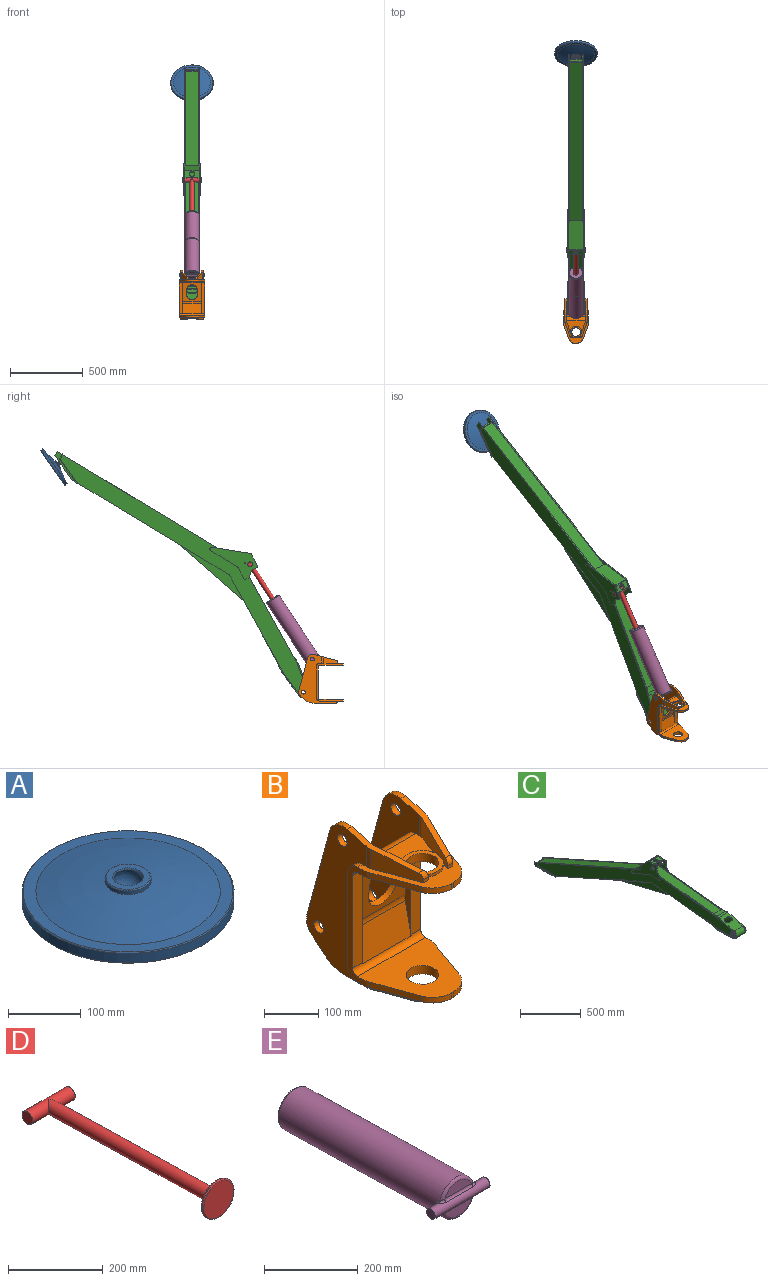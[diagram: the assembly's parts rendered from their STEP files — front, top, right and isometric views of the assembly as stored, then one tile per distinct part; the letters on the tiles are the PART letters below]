
ASSEMBLY  parts=5 mates=5
PART A: 11 faces, bbox 292.1x292.1x54.5 mm
  f0: plane 289.15x289.15mm, normal (0,0,-1), area 65666.8mm2, adj f7
  f1: cylinder r=146.05mm len=292.1mm, axis (0,0,1), area 14777.2mm2, adj f7,f8
  f2: plane 289.15x289.15mm, normal (0,0,1), area 14996mm2, adj f3,f8
  f3: revolved ~254x254mm, area 48420.7mm2, adj f2,f4
  f4: cylinder r=31.75mm len=63.5mm, axis (0,0,1), area 1255.8mm2, adj f3,f9
  f5: plane 60.55x60.55mm, normal (0,0,1), area 1477.2mm2, adj f9,f10
  f6: sphere r=21.59mm, area 4102.8mm2, adj f10
  f7: cone r=146.05mm half-angle=45deg, axis (0,0,1), area 1902.5mm2, adj f0,f1
  f8: cone r=144.58mm half-angle=45deg, axis (0,0,-1), area 1902.5mm2, adj f1,f2
  f9: cone r=30.28mm half-angle=45deg, axis (0,0,-1), area 406mm2, adj f4,f5
  f10: cone r=19.78mm half-angle=33.2deg, axis (0,0,1), area 317mm2, adj f5,f6
PART B: 98 faces, bbox 177.8x305.8x334 mm
  f0: plane 213.74x16.26mm, normal (1,0,0), area 1741.2mm2, adj f36,f38,f39,f87,f88,f89
  f1: plane 334.04x155.74mm, normal (1,0,0), area 29123.4mm2, adj f6,f7,f8,f10,f11,f12,f13,f14
  f2: plane 334.04x155.74mm, normal (-1,0,0), area 29123.4mm2, adj f40,f42,f67,f68,f72,f73,f74,f75
  f3: plane 213.74x16.26mm, normal (-1,0,0), area 1741.2mm2, adj f4,f38,f39,f87,f88,f89
  f4: plane 209.55x25.4mm, normal (0,-1,0), area 5322.6mm2, adj f3,f32,f38,f39
  f5: plane 103.39x44.26mm, normal (0.94,0.34,0), area 3175.5mm2, adj f8,f9,f22,f24,f25,f40,f47,f48
  f6: cylinder r=12.7mm len=25.4mm, axis (-1,0,0), area 1013.4mm2, adj f1,f16
  f7: cylinder r=12.7mm len=25.4mm, axis (-1,0,0), area 1013.4mm2, adj f1,f16
  f8: plane 151.55x48mm, normal (0,-0.26,0.97), area 2071.1mm2, adj f1,f5,f10,f16,f18,f19,f22,f94
  f9: plane 13.5x6.81mm, normal (0,-1,0), area 92mm2, adj f5,f19,f24,f94
  f10: cylinder r=38.1mm len=46.66mm, axis (-1,0,0), area 760.1mm2, adj f1,f8,f11,f16
  f11: plane 219.46x58.81mm, normal (0,0.97,0.26), area 2885.5mm2, adj f1,f10,f12,f16
  f12: cylinder r=38.1mm len=39.05mm, axis (-1,0,0), area 548.9mm2, adj f1,f11,f13,f16
  f13: plane 35.11x29.46mm, normal (0,0.64,-0.77), area 582.1mm2, adj f1,f12,f14,f16
  f14: cylinder r=76.2mm len=48.98mm, axis (-1,0,0), area 675.6mm2, adj f1,f13,f15,f16
  f15: plane 157.33x46.82mm, normal (0,0,-1), area 2071.4mm2, adj f1,f14,f16,f17,f20,f21,f23,f95
  f16: plane 334.04x155.74mm, normal (-1,0,0), area 30898mm2, adj f6,f7,f8,f10,f11,f12,f13,f14
  f17: cylinder r=38.1mm len=12.9mm, axis (0,0,-1), area 167.1mm2, adj f15,f16,f20,f26
  f18: cylinder r=38.1mm len=46.56mm, axis (0,0,-1), area 589.6mm2, adj f8,f16,f19,f24
  f19: plane 99.09x43.11mm, normal (-0.94,-0.34,0), area 3122.2mm2, adj f8,f9,f18,f24,f94
  f20: plane 99.09x35.64mm, normal (-0.94,-0.34,0), area 1300.6mm2, adj f15,f17,f26,f95
  f21: cylinder r=25.4mm len=12.7mm, axis (0,0,-1), area 111.4mm2, adj f1,f15,f23,f42
  f22: cylinder r=25.4mm len=46.56mm, axis (0,0,-1), area 398.2mm2, adj f1,f5,f8,f40
  f23: plane 103.39x37.19mm, normal (0.94,0.34,0), area 1212.3mm2, adj f15,f21,f26,f27,f42,f49,f50,f95
  f24: plane 177.8x159.66mm, normal (0,0,1), area 6507mm2, adj f5,f9,f16,f18,f19,f25,f29,f32
  f25: cylinder r=38.89mm len=62.11mm, axis (0,0,-1), area 456.7mm2, adj f5,f24,f48,f63
  f26: plane 177.8x159.66mm, normal (0,0,-1), area 6507mm2, adj f16,f17,f20,f23,f30,f31,f32,f34
  f27: cylinder r=38.89mm len=77.78mm, axis (0,0,1), area 797.8mm2, adj f23,f42,f50,f69
  f28: plane 209.55x12.7mm, normal (0,1,0), area 2661.3mm2, adj f29,f30,f32,f80
  f29: cylinder r=25.4mm len=25.4mm, axis (-1,0,0), area 506.7mm2, adj f24,f28,f32,f80
  f30: cylinder r=25.4mm len=25.4mm, axis (-1,0,0), area 506.7mm2, adj f26,f28,f32,f80
  f31: plane 12.7x4.77mm, normal (0,-1,0), area 60.6mm2, adj f26,f37,f59,f60
  f32: plane 260.35x34.98mm, normal (1,0,0), area 3664.7mm2, adj f4,f24,f26,f28,f29,f30,f35,f37
  f33: plane 12.7x4.77mm, normal (0,-1,0), area 60.6mm2, adj f24,f35,f55,f56
  f34: plane 260.35x34.98mm, normal (-1,0,0), area 3664.7mm2, adj f24,f26,f35,f36,f37,f38,f39,f41
  f35: plane 177.8x159.66mm, normal (0,0,-1), area 17911.7mm2, adj f32,f33,f34,f38,f46,f53,f54,f55
  f36: plane 209.55x25.4mm, normal (0,-1,0), area 5322.6mm2, adj f0,f34,f38,f39
  f37: plane 177.8x159.66mm, normal (0,0,1), area 17911.7mm2, adj f31,f32,f34,f39,f45,f51,f52,f57
  f38: cylinder r=12.7mm len=177.8mm, axis (-1,0,0), area 3349.9mm2, adj f0,f3,f4,f32,f34,f35,f36,f89
  f39: cylinder r=12.7mm len=177.8mm, axis (-1,0,0), area 3209.1mm2, adj f0,f3,f4,f32,f34,f36,f37,f87
  f40: plane 127x82.53mm, normal (0,0,1), area 6280mm2, adj f1,f2,f5,f22,f47,f63,f67,f85
  f41: plane 209.55x12.7mm, normal (0,1,0), area 2661.3mm2, adj f16,f34,f43,f44
  f42: plane 127x82.53mm, normal (0,0,-1), area 6280mm2, adj f1,f2,f21,f23,f27,f68,f69,f86
  f43: cylinder r=25.4mm len=25.4mm, axis (-1,0,0), area 506.7mm2, adj f16,f24,f34,f41
  f44: cylinder r=25.4mm len=25.4mm, axis (-1,0,0), area 506.7mm2, adj f16,f26,f34,f41
  f45: cylinder r=30mm len=60mm, axis (0,0,1), area 3590.8mm2, adj f37,f50
  f46: cylinder r=30mm len=60mm, axis (0,0,1), area 3590.8mm2, adj f35,f48
  f47: cylinder r=38.89mm len=77.78mm, axis (0,0,-1), area 797.8mm2, adj f5,f40,f48,f63
  f48: plane 77.78x77.78mm, normal (0,0,1), area 1870.2mm2, adj f5,f25,f46,f47,f63
  f49: cylinder r=38.89mm len=62.11mm, axis (0,0,1), area 456.7mm2, adj f23,f26,f50,f69
  f50: plane 77.78x77.78mm, normal (0,0,-1), area 1870.2mm2, adj f23,f27,f45,f49,f69
  f51: plane 99.28x35.71mm, normal (-0.94,-0.34,0), area 1340mm2, adj f26,f37,f59,f61
  f52: plane 99.28x35.71mm, normal (0.94,-0.34,0), area 1340mm2, adj f26,f37,f57,f60
  f53: plane 99.28x35.71mm, normal (-0.94,-0.34,0), area 1340mm2, adj f24,f35,f55,f62
  f54: plane 99.28x35.71mm, normal (0.94,-0.34,0), area 1340mm2, adj f24,f35,f56,f58
  f55: cylinder r=50.8mm len=47.8mm, axis (0,0,1), area 790.6mm2, adj f24,f33,f35,f53
  f56: cylinder r=50.8mm len=47.8mm, axis (0,0,1), area 790.6mm2, adj f24,f33,f35,f54
  f57: cylinder r=50.8mm len=17.19mm, axis (0,0,1), area 222.8mm2, adj f26,f32,f37,f52
  f58: cylinder r=50.8mm len=17.19mm, axis (0,0,-1), area 222.8mm2, adj f24,f32,f35,f54
  f59: cylinder r=50.8mm len=47.8mm, axis (0,0,1), area 790.6mm2, adj f26,f31,f37,f51
  f60: cylinder r=50.8mm len=47.8mm, axis (0,0,1), area 790.6mm2, adj f26,f31,f37,f52
  f61: cylinder r=50.8mm len=17.19mm, axis (0,0,-1), area 222.8mm2, adj f26,f34,f37,f51
  f62: cylinder r=50.8mm len=17.19mm, axis (0,0,1), area 222.8mm2, adj f24,f34,f35,f53
  f63: plane 103.39x44.26mm, normal (-0.94,0.34,0), area 3175.5mm2, adj f24,f25,f40,f47,f48,f66,f67,f77
  f64: cylinder r=38.1mm len=46.56mm, axis (0,0,-1), area 589.6mm2, adj f24,f65,f77,f80
  f65: plane 99.09x43.11mm, normal (0.94,-0.34,0), area 3122.2mm2, adj f24,f64,f66,f77,f96
  f66: plane 13.5x6.81mm, normal (0,-1,0), area 92mm2, adj f24,f63,f65,f96
  f67: cylinder r=25.4mm len=46.56mm, axis (0,0,-1), area 398.2mm2, adj f2,f40,f63,f77
  f68: cylinder r=25.4mm len=12.7mm, axis (0,0,-1), area 111.4mm2, adj f2,f42,f69,f78
  f69: plane 103.39x37.19mm, normal (-0.94,0.34,0), area 1212.3mm2, adj f26,f27,f42,f49,f50,f68,f78,f97
  f70: plane 99.09x35.64mm, normal (0.94,-0.34,0), area 1300.6mm2, adj f26,f71,f78,f97
  f71: cylinder r=38.1mm len=12.9mm, axis (0,0,-1), area 167.1mm2, adj f26,f70,f78,f80
  f72: cylinder r=76.2mm len=48.98mm, axis (-1,0,0), area 675.6mm2, adj f2,f73,f78,f80
  f73: plane 35.11x29.46mm, normal (0,0.64,-0.77), area 582.1mm2, adj f2,f72,f74,f80
  f74: cylinder r=38.1mm len=39.05mm, axis (-1,0,0), area 548.9mm2, adj f2,f73,f75,f80
  f75: plane 219.46x58.81mm, normal (0,0.97,0.26), area 2885.5mm2, adj f2,f74,f76,f80
  f76: cylinder r=38.1mm len=46.66mm, axis (-1,0,0), area 760.1mm2, adj f2,f75,f77,f80
  f77: plane 151.55x48mm, normal (0,-0.26,0.97), area 2071.1mm2, adj f2,f63,f64,f65,f67,f76,f80,f96
  f78: plane 157.33x46.82mm, normal (0,0,-1), area 2071.4mm2, adj f2,f68,f69,f70,f71,f72,f80,f97
  f79: cylinder r=12.7mm len=25.4mm, axis (-1,0,0), area 1013.4mm2, adj f2,f80
  f80: plane 334.04x155.74mm, normal (1,0,0), area 30898mm2, adj f24,f26,f28,f29,f30,f64,f71,f72
  f81: cylinder r=12.7mm len=25.4mm, axis (-1,0,0), area 1013.4mm2, adj f2,f80
  f82: plane 127x72.57mm, normal (0,0.98,-0.21), area 9422.1mm2, adj f1,f2,f83,f86
  f83: cylinder r=50.8mm len=127mm, axis (1,0,0), area 2139.4mm2, adj f1,f2,f82,f84
  f84: plane 128.61x127mm, normal (0,0.99,0.12), area 9763.7mm2, adj f1,f2,f83,f85,f90,f91,f92,f93
  f85: cylinder r=25.4mm len=127mm, axis (1,0,0), area 4673mm2, adj f1,f2,f40,f84
  f86: cylinder r=25.4mm len=127mm, axis (1,0,0), area 4391.5mm2, adj f1,f2,f42,f82
  f87: plane 127x72.57mm, normal (0,-0.98,0.21), area 9422.1mm2, adj f0,f3,f39,f88
  f88: cylinder r=38.1mm len=127mm, axis (1,0,0), area 1604.6mm2, adj f0,f3,f87,f89
  f89: plane 128.61x127mm, normal (0,-0.99,-0.12), area 9763.7mm2, adj f0,f3,f38,f88,f90,f91,f92,f93
  f90: plane 29.31x16.01mm, normal (-1,0,0), area 355.2mm2, adj f84,f89,f91,f93
  f91: cylinder r=38.1mm len=76.2mm, axis (0,0.99,0.12), area 1520.1mm2, adj f84,f89,f90,f92
  f92: plane 29.31x16.01mm, normal (1,0,0), area 355.2mm2, adj f84,f89,f91,f93
  f93: cylinder r=38.1mm len=76.2mm, axis (0,0.99,0.12), area 1520.1mm2, adj f84,f89,f90,f92
  f94: cylinder r=12.7mm len=16.88mm, axis (1,0,0), area 224.4mm2, adj f5,f8,f9,f19
  f95: cylinder r=12.7mm len=18.07mm, axis (1,0,0), area 269.2mm2, adj f15,f20,f23,f26
  f96: cylinder r=12.7mm len=16.88mm, axis (1,0,0), area 224.4mm2, adj f63,f65,f66,f77
  f97: cylinder r=12.7mm len=18.07mm, axis (1,0,0), area 269.2mm2, adj f26,f69,f70,f78
PART C: 172 faces, bbox 127x2358.1x762.4 mm
  f0: cylinder r=9.53mm len=19.05mm, axis (0,0,1), area 271.4mm2, adj f169,f170
  f1: sphere r=12.7mm, area 872.5mm2, adj f170,f171
  f2: plane 2312.35x598.31mm, normal (-1,0,0), area 247360.8mm2, adj f3,f5,f17,f24,f25,f41,f42,f56
  f3: plane 530.06x57.29mm, normal (0,0.11,-0.99), area 3305.6mm2, adj f2,f40,f90,f96,f112
  f4: plane 750.78x331.63mm, normal (0,-0.4,-0.91), area 5211.8mm2, adj f17,f51,f52,f108
  f5: plane 762.53x82.41mm, normal (0,-0.11,0.99), area 4790.4mm2, adj f2,f40,f41,f92,f94,f132
  f6: plane 762.53x82.41mm, normal (0,-0.11,0.99), area 4790.4mm2, adj f51,f52,f53,f93,f95,f131
  f7: plane 25.33x11.19mm, normal (0,-0.4,-0.91), area 175.9mm2, adj f9,f10,f11,f26
  f8: plane 33.6x14.84mm, normal (0,0.4,0.91), area 233.3mm2, adj f9,f10,f12,f28
  f9: plane 238.23x45.76mm, normal (1,0,0), area 3495.7mm2, adj f7,f8,f11,f12,f19,f26,f28
  f10: plane 238.23x45.76mm, normal (-1,0,0), area 3495.7mm2, adj f7,f8,f11,f12,f15,f26,f28
  f11: plane 199.24x6.35mm, normal (0,0,-1), area 1265.2mm2, adj f7,f9,f10,f12
  f12: plane 30.91x13.66mm, normal (0,0.91,-0.4), area 214.6mm2, adj f8,f9,f10,f11
  f13: plane 173.96x88.9mm, normal (0,0,1), area 15464.7mm2, adj f14,f36,f40,f52
  f14: cylinder r=3.17mm len=88.9mm, axis (1,0,0), area 326mm2, adj f13,f16,f40,f52
  f15: cylinder r=9.53mm len=88.9mm, axis (1,0,0), area 977.9mm2, adj f10,f26,f28,f46
  f16: plane 88.9x20.18mm, normal (0,-0.91,0.4), area 1961mm2, adj f14,f30,f40,f52
  f17: plane 200.03x106.68mm, normal (0,0,1), area 1968.3mm2, adj f2,f4,f18,f21,f22,f23,f24,f34
  f18: cylinder r=3.17mm len=2.9mm, axis (1,0,0), area 9.3mm2, adj f17,f23,f25,f51
  f19: cylinder r=9.53mm len=8.71mm, axis (1,0,0), area 27.9mm2, adj f9,f23,f26,f28
  f20: plane 96.52x5.81mm, normal (0,0.4,0.91), area 612.9mm2, adj f25,f28,f166,f167
  f21: plane 220.47x34.81mm, normal (-1,0,0), area 1501.2mm2, adj f17,f22,f24,f25,f26,f27,f28,f167
  f22: plane 106.68x6.35mm, normal (0,-1,0), area 677.4mm2, adj f17,f21,f23,f26
  f23: plane 220.47x34.81mm, normal (1,0,0), area 1501.2mm2, adj f17,f18,f19,f22,f25,f26,f28,f166
  f24: cylinder r=3.17mm len=2.9mm, axis (1,0,0), area 9.3mm2, adj f2,f17,f21,f25
  f25: plane 106.68x31.21mm, normal (0,-0.91,0.4), area 702.6mm2, adj f2,f18,f20,f21,f23,f24,f32,f40
  f26: plane 200.03x106.68mm, normal (0,0,-1), area 18328.7mm2, adj f7,f9,f10,f15,f19,f21,f22,f23
  f27: cylinder r=9.53mm len=8.71mm, axis (1,0,0), area 27.9mm2, adj f21,f26,f28,f45
  f28: plane 106.68x31.21mm, normal (0,0.91,-0.4), area 3228.1mm2, adj f8,f9,f10,f15,f19,f20,f21,f23
  f29: plane 792.4x88.9mm, normal (0,0.11,-0.99), area 70854.5mm2, adj f30,f38,f40,f52
  f30: plane 1309.57x578.45mm, normal (0,-0.4,-0.91), area 127272.8mm2, adj f16,f29,f40,f52
  f31: plane 794.09x88.9mm, normal (0,-0.11,0.99), area 71005.7mm2, adj f32,f38,f40,f52
  f32: plane 1311.13x579.14mm, normal (0,0.4,0.91), area 127424mm2, adj f25,f31,f40,f52
  f33: plane 765.33x88.9mm, normal (0,0.11,-0.99), area 68434.3mm2, adj f34,f37,f40,f52
  f34: plane 1124.23x496.59mm, normal (0,-0.4,-0.91), area 109260.2mm2, adj f17,f33,f40,f52
  f35: plane 767.02x88.9mm, normal (0,-0.11,0.99), area 68585.6mm2, adj f36,f37,f40,f52
  f36: plane 1138.94x503.08mm, normal (0,0.4,0.91), area 110689.5mm2, adj f13,f35,f40,f52
  f37: plane 88.9x6.31mm, normal (0,-0.99,-0.11), area 564.5mm2, adj f33,f35,f40,f52
  f38: plane 88.9x6.31mm, normal (0,-0.99,-0.11), area 564.5mm2, adj f29,f31,f40,f52
  f39: cylinder r=12.7mm len=25.4mm, axis (1,0,0), area 1520.1mm2, adj f40,f57
  f40: plane 2312.35x610.27mm, normal (1,0,0), area 254834.7mm2, adj f3,f5,f13,f14,f16,f17,f25,f29
  f41: plane 1311.91x579.49mm, normal (0,0.4,0.91), area 9107.1mm2, adj f2,f5,f25,f40,f132
  f42: plane 750.78x331.63mm, normal (0,-0.4,-0.91), area 5211.8mm2, adj f2,f17,f40,f112
  f43: plane 25.33x11.19mm, normal (0,-0.4,-0.91), area 175.9mm2, adj f26,f45,f46,f47
  f44: plane 33.6x14.84mm, normal (0,0.4,0.91), area 233.3mm2, adj f28,f45,f46,f48
  f45: plane 238.23x45.76mm, normal (-1,0,0), area 3495.7mm2, adj f26,f27,f28,f43,f44,f47,f48
  f46: plane 238.23x45.76mm, normal (1,0,0), area 3495.7mm2, adj f15,f26,f28,f43,f44,f47,f48
  f47: plane 199.24x6.35mm, normal (0,0,-1), area 1265.2mm2, adj f43,f45,f46,f48
  f48: plane 30.91x13.66mm, normal (0,0.91,-0.4), area 214.6mm2, adj f44,f45,f46,f47
  f49: plane 530.06x57.29mm, normal (0,0.11,-0.99), area 3305.6mm2, adj f51,f52,f91,f97,f108
  f50: cylinder r=12.7mm len=25.4mm, axis (-1,0,0), area 1520.1mm2, adj f52,f55
  f51: plane 2312.35x598.31mm, normal (1,0,0), area 247360.8mm2, adj f4,f6,f17,f18,f25,f49,f53,f54
  f52: plane 2312.35x610.27mm, normal (-1,0,0), area 254834.7mm2, adj f4,f6,f13,f14,f16,f17,f25,f29
  f53: plane 1311.91x579.49mm, normal (0,0.4,0.91), area 9107.1mm2, adj f6,f25,f51,f52,f131
  f54: cylinder r=25.4mm len=50.8mm, axis (-1,0,0), area 2026.8mm2, adj f51,f55
  f55: plane 50.8x50.8mm, normal (1,0,0), area 1520.1mm2, adj f50,f54
  f56: cylinder r=25.4mm len=50.8mm, axis (1,0,0), area 2026.8mm2, adj f2,f57
  f57: plane 50.8x50.8mm, normal (-1,0,0), area 1520.1mm2, adj f39,f56
  f58: plane 181.4x44.12mm, normal (0,0.24,-0.97), area 1185.5mm2, adj f2,f72,f79,f81
  f59: plane 181.4x88.9mm, normal (0,0.24,-0.97), area 13279.5mm2, adj f40,f52,f66,f70,f98,f99,f100,f101
  f60: plane 186.64x88.9mm, normal (0,0.02,1), area 13279.5mm2, adj f40,f52,f64,f66,f102,f103,f104,f105
  f61: plane 186.64x6.35mm, normal (0,0.02,1), area 1185.5mm2, adj f51,f65,f67,f74
  f62: plane 88.9x37.88mm, normal (0,-0.11,0.99), area 3382.5mm2, adj f40,f52,f64,f75,f96,f97
  f63: plane 12.63x3.18mm, normal (0,-0.11,0.99), area 20.2mm2, adj f2,f77,f90
  f64: cylinder r=152.4mm len=88.9mm, axis (1,0,0), area 1773.5mm2, adj f40,f52,f60,f62
  f65: cylinder r=152.4mm len=19.92mm, axis (1,0,0), area 106.5mm2, adj f51,f61,f74,f76,f91
  f66: cylinder r=31.75mm len=88.9mm, axis (1,0,0), area 8128.4mm2, adj f40,f52,f59,f60
  f67: cylinder r=31.75mm len=62.59mm, axis (1,0,0), area 580.6mm2, adj f51,f61,f74,f82
  f68: plane 12.63x3.18mm, normal (0,0.11,-0.99), area 20.2mm2, adj f2,f81,f92
  f69: plane 88.9x37.88mm, normal (0,0.11,-0.99), area 3382.5mm2, adj f40,f52,f70,f73,f94,f95
  f70: cylinder r=152.4mm len=88.9mm, axis (1,0,0), area 1773.5mm2, adj f40,f52,f59,f69
  f71: cylinder r=152.4mm len=19.64mm, axis (1,0,0), area 106.5mm2, adj f51,f74,f80,f82,f93
  f72: plane 231.92x125.31mm, normal (-1,0,0), area 3106.8mm2, adj f58,f77,f78,f79,f81,f84,f85,f86
  f73: plane 80.97x6.31mm, normal (0,0.99,0.11), area 514.1mm2, adj f69,f87,f94,f95
  f74: plane 231.92x125.31mm, normal (1,0,0), area 3106.8mm2, adj f61,f65,f67,f71,f82,f84,f85,f86
  f75: plane 80.97x6.31mm, normal (0,0.99,0.11), area 514.1mm2, adj f62,f83,f96,f97
  f76: plane 12.63x3.18mm, normal (0,-0.11,0.99), area 20.2mm2, adj f51,f65,f91
  f77: cylinder r=152.4mm len=19.92mm, axis (1,0,0), area 106.5mm2, adj f2,f63,f72,f78,f90
  f78: plane 186.64x6.35mm, normal (0,0.02,1), area 1185.5mm2, adj f2,f72,f77,f79
  f79: cylinder r=31.75mm len=62.59mm, axis (1,0,0), area 580.6mm2, adj f2,f58,f72,f78
  f80: plane 12.63x3.18mm, normal (0,0.11,-0.99), area 20.2mm2, adj f51,f71,f93
  f81: cylinder r=152.4mm len=19.64mm, axis (1,0,0), area 106.5mm2, adj f2,f58,f68,f72,f92
  f82: plane 181.4x44.12mm, normal (0,0.24,-0.97), area 1185.5mm2, adj f51,f67,f71,f74
  f83: plane 107.95x37.88mm, normal (0,0.11,-0.99), area 3743.9mm2, adj f75,f84,f90,f91,f96,f97
  f84: cylinder r=158.75mm len=114.3mm, axis (1,0,0), area 2334.8mm2, adj f72,f74,f83,f85,f90,f91
  f85: plane 186.64x114.3mm, normal (0,-0.02,-1), area 18021.4mm2, adj f72,f74,f84,f86,f102,f103,f104,f105
  f86: cylinder r=38.1mm len=114.3mm, axis (1,0,0), area 12541mm2, adj f72,f74,f85,f89
  f87: plane 107.95x37.88mm, normal (0,-0.11,0.99), area 3743.9mm2, adj f73,f88,f92,f93,f94,f95
  f88: cylinder r=158.75mm len=114.3mm, axis (1,0,0), area 2334.8mm2, adj f72,f74,f87,f89,f92,f93
  f89: plane 181.4x114.3mm, normal (0,-0.24,0.97), area 18021.4mm2, adj f72,f74,f86,f88,f98,f99,f100,f101
  f90: plane 47.42x11.74mm, normal (-0.97,0.24,0.03), area 307.4mm2, adj f3,f63,f72,f77,f83,f84,f96
  f91: plane 47.42x11.74mm, normal (0.97,0.24,0.03), area 307.4mm2, adj f49,f65,f74,f76,f83,f84,f97
  f92: plane 47.31x11.89mm, normal (-0.97,0.24,0.03), area 307.4mm2, adj f5,f68,f72,f81,f87,f88,f94
  f93: plane 47.31x11.89mm, normal (0.97,0.24,0.03), area 307.4mm2, adj f6,f71,f74,f80,f87,f88,f95
  f94: cylinder r=5.08mm len=6.73mm, axis (0,0.11,-0.99), area 42.8mm2, adj f5,f69,f73,f87,f92
  f95: cylinder r=5.08mm len=6.73mm, axis (0,-0.11,0.99), area 42.8mm2, adj f6,f69,f73,f87,f93
  f96: cylinder r=5.08mm len=6.73mm, axis (0,0.11,-0.99), area 42.8mm2, adj f3,f62,f75,f83,f90
  f97: cylinder r=5.08mm len=6.73mm, axis (0,-0.11,0.99), area 42.8mm2, adj f49,f62,f75,f83,f91
  f98: plane 25.4x6.17mm, normal (0,-0.97,-0.24), area 161.3mm2, adj f59,f89,f99,f101
  f99: cylinder r=25.4mm len=50.86mm, axis (0,-0.24,0.97), area 506.7mm2, adj f59,f89,f98,f100
  f100: plane 25.4x6.17mm, normal (0,0.97,0.24), area 161.3mm2, adj f59,f89,f99,f101
  f101: cylinder r=25.4mm len=50.86mm, axis (0,-0.24,0.97), area 506.7mm2, adj f59,f89,f98,f100
  f102: plane 25.4x6.35mm, normal (0,-1,0.02), area 161.3mm2, adj f60,f85,f103,f105
  f103: cylinder r=25.4mm len=50.93mm, axis (0,-0.02,-1), area 506.7mm2, adj f60,f85,f102,f104
  f104: plane 25.4x6.35mm, normal (0,1,-0.02), area 161.3mm2, adj f60,f85,f103,f105
  f105: cylinder r=25.4mm len=50.93mm, axis (0,-0.02,-1), area 506.7mm2, adj f60,f85,f102,f104
  f106: plane 568.13x161.71mm, normal (1,0,0), area 20331.5mm2, adj f107,f108,f109
  f107: plane 202.02x21.83mm, normal (0,-0.11,0.99), area 516.1mm2, adj f51,f106,f108,f109
  f108: plane 568.13x139.88mm, normal (0,-0.24,-0.97), area 5201.5mm2, adj f4,f49,f52,f106,f107,f109
  f109: plane 366.1x161.71mm, normal (0,0.4,0.91), area 1016.6mm2, adj f51,f106,f107,f108
  f110: plane 568.13x161.71mm, normal (-1,0,0), area 20331.5mm2, adj f111,f112,f113
  f111: plane 202.02x21.83mm, normal (0,-0.11,0.99), area 516.1mm2, adj f2,f110,f112,f113
  f112: plane 568.13x139.88mm, normal (0,-0.24,-0.97), area 5201.5mm2, adj f3,f40,f42,f110,f111,f113
  f113: plane 366.1x161.71mm, normal (0,0.4,0.91), area 1016.6mm2, adj f2,f110,f111,f112
  f114: plane 29.61x23.83mm, normal (0,-0.78,0.63), area 241.4mm2, adj f115,f128,f130,f131
  f115: cylinder r=5.08mm len=6.35mm, axis (-1,0,0), area 25.3mm2, adj f51,f114,f116,f130,f131
  f116: plane 30.74x6.35mm, normal (0,-0.99,-0.11), area 196.3mm2, adj f51,f115,f117,f130
  f117: cylinder r=5.08mm len=6.35mm, axis (-1,0,0), area 50.7mm2, adj f51,f116,f118,f130
  f118: plane 89.16x9.64mm, normal (0,0.11,-0.99), area 569.4mm2, adj f51,f117,f119,f130
  f119: cylinder r=25.4mm len=12.99mm, axis (-1,0,0), area 84.5mm2, adj f51,f118,f120,f130
  f120: plane 190.45x84.13mm, normal (0,-0.4,-0.91), area 1322.1mm2, adj f51,f119,f121,f130
  f121: cylinder r=12.7mm len=21.55mm, axis (-1,0,0), area 222.4mm2, adj f51,f120,f122,f130
  f122: plane 192.47x186.96mm, normal (0,0.72,0.7), area 1703.8mm2, adj f51,f121,f123,f130,f131
  f123: cylinder r=5.08mm len=6.35mm, axis (-1,0,0), area 29.3mm2, adj f122,f124,f130,f131
  f124: plane 89.71x9.7mm, normal (0,-0.11,0.99), area 573mm2, adj f123,f125,f130,f131
  f125: cylinder r=8.89mm len=9.79mm, axis (-1,0,0), area 88.7mm2, adj f124,f126,f130,f131
  f126: plane 31.21x6.35mm, normal (0,-0.99,-0.11), area 199.3mm2, adj f125,f128,f130,f131
  f127: cylinder r=6.35mm len=12.7mm, axis (-1,0,0), area 253.4mm2, adj f130,f131
  f128: cylinder r=25.4mm len=18.66mm, axis (-1,0,0), area 126.7mm2, adj f114,f126,f130,f131
  f129: cylinder r=15.88mm len=31.75mm, axis (-1,0,0), area 633.4mm2, adj f130,f131
  f130: plane 319.38x215.56mm, normal (1,0,0), area 28558.8mm2, adj f114,f115,f116,f117,f118,f119,f120,f121
  f131: plane 290.19x167.92mm, normal (-1,0,0), area 14445.6mm2, adj f6,f53,f114,f115,f122,f123,f124,f125
  f132: plane 290.19x167.92mm, normal (1,0,0), area 14445.6mm2, adj f5,f41,f133,f134,f141,f142,f143,f144
  f133: plane 29.61x23.83mm, normal (0,-0.78,0.63), area 241.4mm2, adj f132,f134,f147,f149
  f134: cylinder r=5.08mm len=6.35mm, axis (1,0,0), area 25.3mm2, adj f2,f132,f133,f135,f149
  f135: plane 30.74x6.35mm, normal (0,-0.99,-0.11), area 196.3mm2, adj f2,f134,f136,f149
  f136: cylinder r=5.08mm len=6.35mm, axis (1,0,0), area 50.7mm2, adj f2,f135,f137,f149
  f137: plane 89.16x9.64mm, normal (0,0.11,-0.99), area 569.4mm2, adj f2,f136,f138,f149
  f138: cylinder r=25.4mm len=12.99mm, axis (1,0,0), area 84.5mm2, adj f2,f137,f139,f149
  f139: plane 190.45x84.13mm, normal (0,-0.4,-0.91), area 1322.1mm2, adj f2,f138,f140,f149
  f140: cylinder r=12.7mm len=21.55mm, axis (1,0,0), area 222.4mm2, adj f2,f139,f141,f149
  f141: plane 192.47x186.96mm, normal (0,0.72,0.7), area 1703.8mm2, adj f2,f132,f140,f142,f149
  f142: cylinder r=5.08mm len=6.35mm, axis (1,0,0), area 29.3mm2, adj f132,f141,f143,f149
  f143: plane 89.71x9.7mm, normal (0,-0.11,0.99), area 573mm2, adj f132,f142,f144,f149
  f144: cylinder r=8.89mm len=9.79mm, axis (1,0,0), area 88.7mm2, adj f132,f143,f145,f149
  f145: plane 31.21x6.35mm, normal (0,-0.99,-0.11), area 199.3mm2, adj f132,f144,f147,f149
  f146: cylinder r=6.35mm len=12.7mm, axis (1,0,0), area 253.4mm2, adj f132,f149
  f147: cylinder r=25.4mm len=18.66mm, axis (1,0,0), area 126.7mm2, adj f132,f133,f145,f149
  f148: cylinder r=15.88mm len=31.75mm, axis (1,0,0), area 633.4mm2, adj f132,f149
  f149: plane 319.38x215.56mm, normal (-1,0,0), area 28558.8mm2, adj f133,f134,f135,f136,f137,f138,f139,f140
  f150: plane 10.53x6.31mm, normal (0,-0.99,-0.11), area 66.9mm2, adj f132,f154,f155,f162
  f151: plane 144.56x140.42mm, normal (0,-0.72,-0.7), area 20314mm2, adj f131,f132,f154,f157,f158,f159
  f152: plane 144.56x140.42mm, normal (0,0.72,0.7), area 20314mm2, adj f131,f132,f156,f157,f158,f159
  f153: plane 10.53x6.31mm, normal (0,-0.99,-0.11), area 66.9mm2, adj f131,f154,f155,f160
  f154: plane 101.6x56.65mm, normal (0,0.11,-0.99), area 4169.4mm2, adj f131,f132,f150,f151,f153,f160,f161,f162
  f155: plane 101.6x56.65mm, normal (0,-0.11,0.99), area 4169.4mm2, adj f131,f132,f150,f153,f156,f160,f161,f162
  f156: cylinder r=6.35mm len=101.6mm, axis (1,0,0), area 585.5mm2, adj f131,f132,f152,f155
  f157: plane 76.2x4.56mm, normal (0,0.7,-0.72), area 483.9mm2, adj f151,f152,f158,f159
  f158: plane 13.53x13.4mm, normal (-0.71,0.49,-0.51), area 114mm2, adj f132,f151,f152,f157
  f159: plane 13.53x13.4mm, normal (0.71,0.49,-0.51), area 114mm2, adj f131,f151,f152,f157
  f160: plane 6.41x1.61mm, normal (-0.98,-0.17,-0.02), area 6mm2, adj f153,f154,f155,f161
  f161: cylinder r=6.35mm len=6.88mm, axis (0,-0.11,0.99), area 56.3mm2, adj f154,f155,f160,f163
  f162: plane 6.41x1.61mm, normal (0.98,-0.17,-0.02), area 6mm2, adj f150,f154,f155,f164
  f163: plane 67.71x6.31mm, normal (0,-0.99,-0.11), area 429.9mm2, adj f154,f155,f161,f164
  f164: cylinder r=6.35mm len=6.88mm, axis (0,-0.11,0.99), area 56.3mm2, adj f154,f155,f162,f163
  f165: cylinder r=19.05mm len=38.56mm, axis (0,-0.11,0.99), area 760.1mm2, adj f154,f155
  f166: cylinder r=5.08mm len=7.86mm, axis (0,-0.91,0.4), area 50.7mm2, adj f20,f23,f25,f28
  f167: cylinder r=5.08mm len=7.86mm, axis (0,0.91,-0.4), area 50.7mm2, adj f20,f21,f25,f28
  f168: sphere r=19.05mm, area 4171.1mm2, adj f169
  f169: torus R=12.06mm, axis (0,0,-1), area 154.7mm2, adj f0,f168
  f170: torus R=12.06mm, axis (0,0,1), area 101.8mm2, adj f0,f1
  f171: torus R=14.76mm, axis (0,0,1), area 378.8mm2, adj f1,f26
PART D: 9 faces, bbox 127x524.9x101.7 mm
  f0: plane 31.75x31.75mm, normal (1,0,0), area 791.7mm2, adj f1
  f1: cylinder r=15.88mm len=127mm, axis (-1,0,0), area 11659.6mm2, adj f0,f2,f3
  f2: plane 31.75x31.75mm, normal (-1,0,0), area 791.7mm2, adj f1
  f3: cylinder r=15.88mm len=502.31mm, axis (0,1,-0.02), area 49035.7mm2, adj f1,f6
  f4: cylinder r=46.99mm len=93.98mm, axis (0,1,-0.02), area 375mm2, adj f7,f8
  f5: plane 88.9x88.88mm, normal (0,-1,0.02), area 6207.2mm2, adj f8
  f6: plane 88.9x88.88mm, normal (0,1,-0.02), area 5415.4mm2, adj f3,f7
  f7: torus R=44.45mm, axis (0,-1,0.02), area 1154.8mm2, adj f4,f6
  f8: torus R=44.45mm, axis (0,-1,0.02), area 1154.8mm2, adj f4,f5
PART E: 28 faces, bbox 165.1x509.1x121.1 mm
  f0: plane 81.32x26.48mm, normal (0,-1,0.02), area 1551.5mm2, adj f3,f20
  f1: plane 81.32x26.48mm, normal (0,-1,0.02), area 1551.5mm2, adj f4,f27
  f2: cylinder r=50.8mm len=486.15mm, axis (0,1,-0.02), area 153866.7mm2, adj f3,f4,f11,f23,f24
  f3: torus R=44.45mm, axis (0,-1,0.02), area 1169.4mm2, adj f0,f2,f21,f22
  f4: torus R=44.45mm, axis (0,-1,0.02), area 1169.4mm2, adj f1,f2,f25,f26
  f5: plane 85.53x32.33mm, normal (0,1,-0.02), area 2040mm2, adj f8,f16
  f6: plane 85.53x32.33mm, normal (0,1,-0.02), area 2040mm2, adj f9,f16
  f7: cylinder r=46.99mm len=485.98mm, axis (0,1,-0.02), area 142680.7mm2, adj f8,f9,f14,f16
  f8: torus R=44.45mm, axis (0,-1,0.02), area 482.6mm2, adj f5,f7,f16
  f9: torus R=44.45mm, axis (0,-1,0.02), area 482.6mm2, adj f6,f7,f16
  f10: plane 91.44x91.42mm, normal (0,1,-0.02), area 5643.5mm2, adj f11,f15
  f11: torus R=45.72mm, axis (0,-1,0.02), area 2454.4mm2, adj f2,f10
  f12: cylinder r=15.88mm len=31.8mm, axis (0,1,-0.02), area 253.4mm2, adj f13,f15
  f13: plane 91.44x91.42mm, normal (0,-1,0.02), area 5775.2mm2, adj f12,f14
  f14: torus R=45.72mm, axis (0,-1,0.02), area 583.2mm2, adj f7,f13
  f15: cone r=17.14mm half-angle=45deg, axis (0,1,-0.02), area 186.3mm2, adj f10,f12
  f16: cylinder r=12.7mm len=93.98mm, axis (-1,0,0), area 2973mm2, adj f5,f6,f7,f8,f9
  f17: plane 25.4x25.4mm, normal (1,0,0), area 506.7mm2, adj f19
  f18: plane 25.4x25.4mm, normal (-1,0,0), area 506.7mm2, adj f19
  f19: cylinder r=12.7mm len=165.1mm, axis (-1,0,0), area 7911.9mm2, adj f17,f18,f20,f21,f22,f23,f24,f25
  f20: cylinder r=6.35mm len=81.32mm, axis (-1,0,0), area 635.6mm2, adj f0,f19,f21,f22
  f21: bspline ~15.89x12.06mm, area 101.6mm2, adj f3,f19,f20,f23
  f22: bspline ~15.89x12.06mm, area 101.6mm2, adj f3,f19,f20,f24
  f23: bspline ~32.95x16.41mm, area 327.5mm2, adj f2,f19,f21,f25
  f24: bspline ~32.95x16.41mm, area 327.5mm2, adj f2,f19,f22,f26
  f25: bspline ~15.89x11.93mm, area 101.6mm2, adj f4,f19,f23,f27
  f26: bspline ~15.89x11.93mm, area 101.6mm2, adj f4,f19,f24,f27
  f27: cylinder r=6.35mm len=81.32mm, axis (-1,0,0), area 635.6mm2, adj f1,f19,f25,f26
PLACE A rot(axis=(1,0,0),55deg) t=(-250.82,-815.28,-904.62)mm
PLACE B t=(-250.82,-1671.28,19.12)mm fixed
PLACE C rot(axis=(1,0,0),55deg) t=(-250.82,-815.28,-904.62)mm
PLACE D rot(axis=(1,0,0),58deg) t=(-250.82,-699.47,-945.32)mm
PLACE E rot(axis=(1,0,0),58deg) t=(-250.82,-583.08,-768.05)mm
MATE fastened C.f0 <-> A.f1  axis (0,-0.82,0.57) through (162.34,1335.6,1936.62)mm
MATE revolute D.f1 <-> C.f129  axis (1,0,0) through (162.34,9.61,1257.23)mm
MATE revolute B.f6 <-> E.f16  axis (-1,0,0) through (162.34,-417.72,606.31)mm
MATE revolute C.f39 <-> B.f7  axis (1,0,0) through (162.34,-356.04,379.44)mm
MATE slider D.f7 <-> E.f11  axis (0,0.55,0.84) through (162.34,-265.73,837.83)mm
